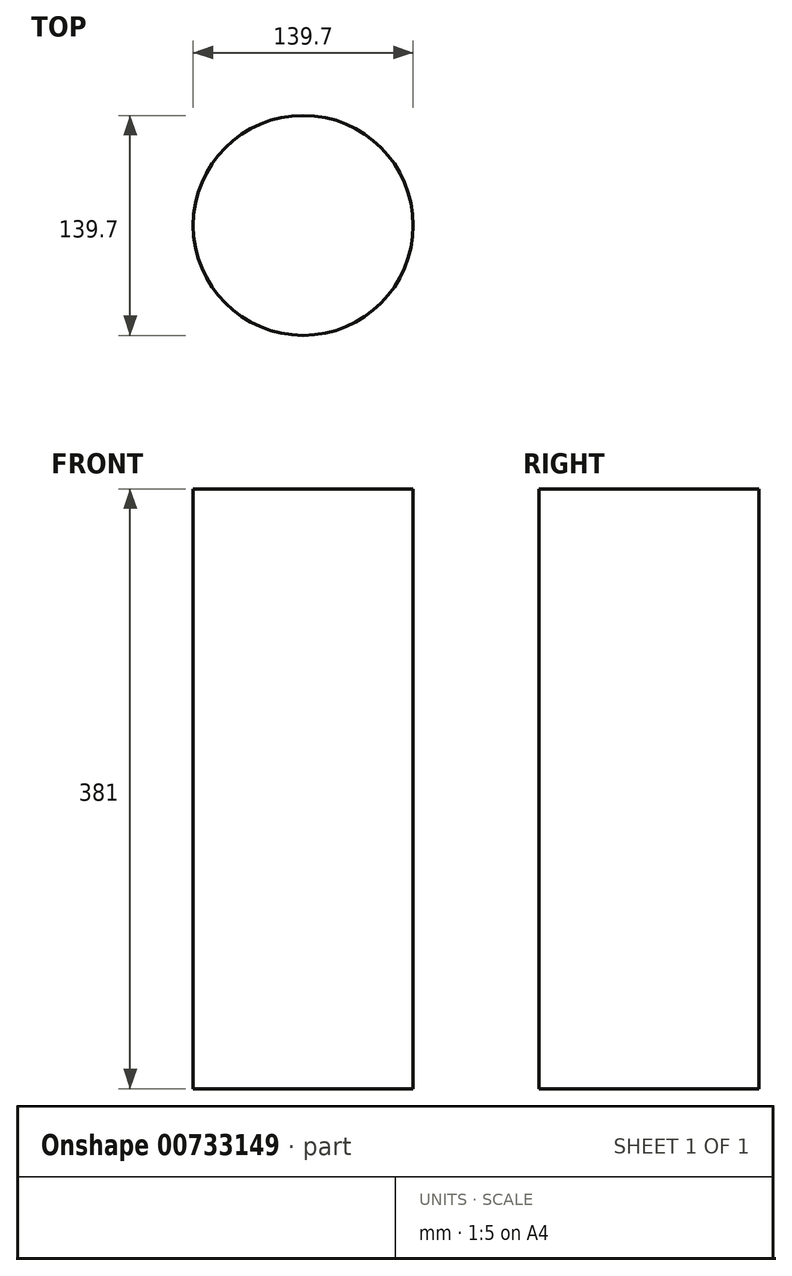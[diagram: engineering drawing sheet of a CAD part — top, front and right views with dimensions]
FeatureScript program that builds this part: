
annotation { "Feature Type Name" : "Feature", "Feature Type Description" : "" }
export const myFeature = defineFeature(function(context is Context, id is Id, definition is map)
    precondition{}
    {
        {
            var Q0;
            Q0=qCreatedBy(makeId("Top.planeOp"),FACE);
            var sketch = newSketch(context, id + "F0", { "sketchPlane" : qUnion([Q0])});
            skCircle(sketch, "E0", {"center": v(0, 5.76) * mm, "radius": 69.85 * mm});
            skSolve(sketch);
        }
        {
            var Q0;
            Q0=makeQuery(id+"F0.imprint","IMPRINT",FACE,{"disambiguationData":[TD([[makeQuery(id+"F0.imprint","IMPRINT",EDGE,{"derivedFrom":sQuery(id+"F0.wireOp",EDGE,"E0")}),1.0]])]});
            extrude(context, id + "F1", {"entities" : qUnion([Q0]), "depth" : 381 * mm, "offsetDistance" : 25.4 * mm});
        }
    });
